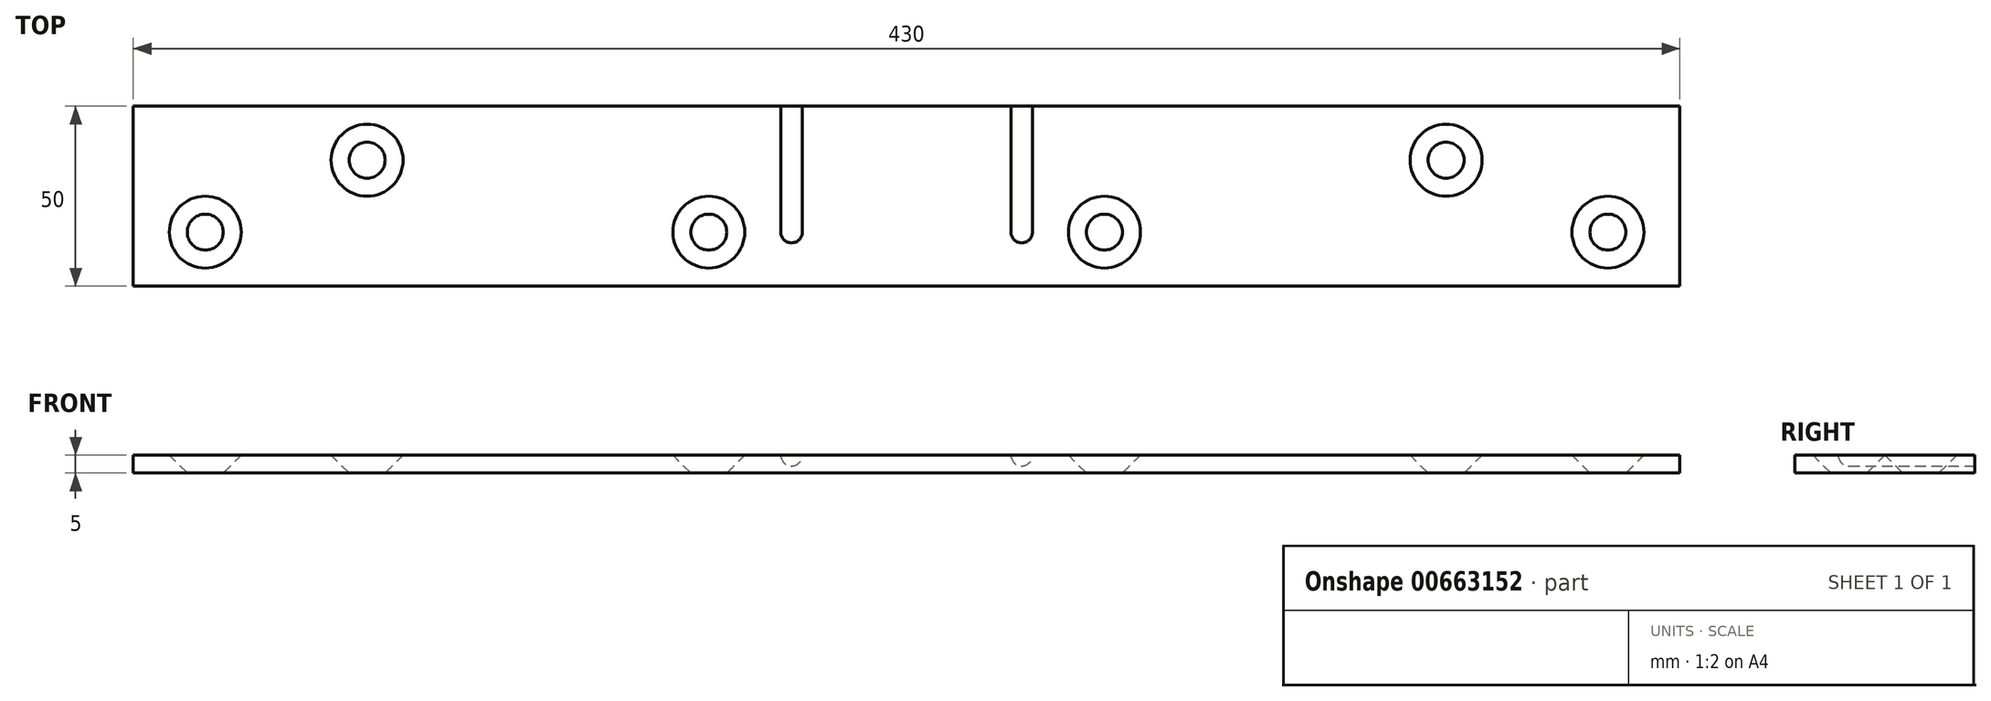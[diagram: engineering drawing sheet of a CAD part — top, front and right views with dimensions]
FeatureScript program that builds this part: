
annotation { "Feature Type Name" : "Feature", "Feature Type Description" : "" }
export const myFeature = defineFeature(function(context is Context, id is Id, definition is map)
    precondition{}
    {
        {
            var Q0;
            Q0=qCreatedBy(makeId("Top.planeOp"),FACE);
            var sketch = newSketch(context, id + "F0", { "sketchPlane" : qUnion([Q0])});
            skLineSegment(sketch, "E0.bottom", {"start": v(-215, 25) * mm, "end": v(215, 25) * mm});
            skLineSegment(sketch, "E0.top", {"start": v(-215, -25) * mm, "end": v(215, -25) * mm});
            skLineSegment(sketch, "E0.left", {"start": v(-215, 25) * mm, "end": v(-215, -25) * mm});
            skLineSegment(sketch, "E0.right", {"start": v(215, 25) * mm, "end": v(215, -25) * mm});
            skPoint(sketch, "E0.middle", {"position": v(0, 0) * mm});
            skSolve(sketch);
        }
        {
            var Q0;
            Q0=makeQuery(id+"F0.imprint","IMPRINT",FACE,{"disambiguationData":[TD([[makeQuery(id+"F0.imprint","IMPRINT",EDGE,{"derivedFrom":sQuery(id+"F0.wireOp",EDGE,"E0.bottom")}),-1.0]])]});
            extrude(context, id + "F1", {"entities" : qUnion([Q0]), "depth" : 5 * mm, "offsetDistance" : 25 * mm});
        }
        {
            var Q0;
            Q0=makeQuery(id+"F1.opExtrude","CAP_FACE",FACE,{"disambiguationData":[OSD([sQuery(id+"F0.wireOp",EDGE,"E0.bottom"),sQuery(id+"F0.wireOp",EDGE,"E0.top"),sQuery(id+"F0.wireOp",EDGE,"E0.left"),sQuery(id+"F0.wireOp",EDGE,"E0.right")])],"isStart":false});
            var sketch = newSketch(context, id + "F2", { "sketchPlane" : qUnion([Q0])});
            skCircle(sketch, "E1", {"center": v(-150, 10) * mm, "radius": 10 * mm});
            skCircle(sketch, "E2", {"center": v(-195, -10) * mm, "radius": 10 * mm});
            skCircle(sketch, "E3.1.0.0", {"center": v(-55, -10) * mm, "radius": 10 * mm});
            skLineSegment(sketch, "E3.direction1", {"start": v(-195, -10) * mm, "end": v(-55, -10) * mm, "construction": true});
            skCircle(sketch, "E4.1.0.0", {"center": v(55, -10) * mm, "radius": 10 * mm});
            skLineSegment(sketch, "E4.direction1", {"start": v(-55, -10) * mm, "end": v(55, -10) * mm, "construction": true});
            skCircle(sketch, "E5", {"center": v(195, -10) * mm, "radius": 10 * mm});
            skCircle(sketch, "E6", {"center": v(150, 10) * mm, "radius": 10 * mm});
            skSolve(sketch);
        }
        {
            var Q0;
            Q0=makeQuery(id+"F2.imprint","IMPRINT",FACE,{"disambiguationData":[TD([[makeQuery(id+"F2.imprint","IMPRINT",EDGE,{"derivedFrom":sQuery(id+"F2.wireOp",EDGE,"E1")}),1.0]])]});
            var Q1;
            Q1=makeQuery(id+"F2.imprint","IMPRINT",FACE,{"disambiguationData":[TD([[makeQuery(id+"F2.imprint","IMPRINT",EDGE,{"derivedFrom":sQuery(id+"F2.wireOp",EDGE,"E3.1.0.0")}),1.0]])]});
            var Q2;
            Q2=makeQuery(id+"F2.imprint","IMPRINT",FACE,{"disambiguationData":[TD([[makeQuery(id+"F2.imprint","IMPRINT",EDGE,{"derivedFrom":sQuery(id+"F2.wireOp",EDGE,"E2")}),1.0]])]});
            var Q3;
            Q3=makeQuery(id+"F2.imprint","IMPRINT",FACE,{"disambiguationData":[TD([[makeQuery(id+"F2.imprint","IMPRINT",EDGE,{"derivedFrom":sQuery(id+"F2.wireOp",EDGE,"E4.1.0.0")}),1.0]])]});
            var Q4;
            Q4=makeQuery(id+"F2.imprint","IMPRINT",FACE,{"disambiguationData":[TD([[makeQuery(id+"F2.imprint","IMPRINT",EDGE,{"derivedFrom":sQuery(id+"F2.wireOp",EDGE,"E5")}),1.0]])]});
            var Q5;
            Q5=makeQuery(id+"F2.imprint","IMPRINT",FACE,{"disambiguationData":[TD([[makeQuery(id+"F2.imprint","IMPRINT",EDGE,{"derivedFrom":sQuery(id+"F2.wireOp",EDGE,"E6")}),1.0]])]});
            var Q6;
            Q6=sQuery(id+"F2.wireOp",EDGE,"E1");
            extrude(context, id + "F3", {"entities" : qUnion([Q0, Q1, Q2, Q3, Q4, Q5]), "operationType" : NewBodyOperationType.REMOVE, "surfaceEntities" : qUnion([Q6]), "endBound" : BoundingType.UP_TO_NEXT, "oppositeDirection" : true, "depth" : 25 * mm, "offsetDistance" : 25 * mm, "hasDraft" : true, "draftAngle" : 45 * degree, "draftPullDirection" : true});
        }
        {
            var Q0;
            Q0=makeQuery(id+"F2.imprint","IMPRINT",FACE,{"disambiguationData":[TD([[makeQuery(id+"F2.imprint","IMPRINT",EDGE,{"derivedFrom":sQuery(id+"F2.wireOp",EDGE,"E1")}),-1.0]])]});
            var sketch = newSketch(context, id + "F4", { "sketchPlane" : qUnion([Q0])});
            skLineSegment(sketch, "E7.bottom", {"start": v(-35, 25) * mm, "end": v(-32, 25) * mm});
            skLineSegment(sketch, "E7.left", {"start": v(-35, 25) * mm, "end": v(-35, -10) * mm});
            skArc(sketch, "E8", {"start": v(-35, -10) * mm, "mid": v(-34.12, -12.12) * mm, "end": v(-32, -13) * mm});
            skLineSegment(sketch, "E9", {"start": v(-32, -13) * mm, "end": v(-32, 25) * mm});
            skSolve(sketch);
        }
        {
            var Q0;
            Q0=makeQuery(id+"F4.imprint","IMPRINT",FACE,{"disambiguationData":[TD([[makeQuery(id+"F4.imprint","IMPRINT",EDGE,{"derivedFrom":sQuery(id+"F4.wireOp",EDGE,"E7.bottom")}),-1.0]])]});
            var Q1;
            Q1=sQuery(id+"F4.wireOp",EDGE,"E9");
            revolve(context, id + "F5", {"operationType" : NewBodyOperationType.REMOVE, "entities" : qUnion([Q0]), "axis" : qUnion([Q1]), "revolveType" : RevolveType.FULL, "oppositeDirection" : true});
        }
        {
            var Q0;
            Q0=makeQuery(id+"F2.imprint","IMPRINT",FACE,{"disambiguationData":[TD([[makeQuery(id+"F2.imprint","IMPRINT",EDGE,{"derivedFrom":sQuery(id+"F2.wireOp",EDGE,"E1")}),-1.0]])]});
            var sketch = newSketch(context, id + "F6", { "sketchPlane" : qUnion([Q0])});
            skLineSegment(sketch, "E10.bottom", {"start": v(29, 25) * mm, "end": v(32, 25) * mm});
            skLineSegment(sketch, "E10.left", {"start": v(29, 25) * mm, "end": v(29, -10) * mm});
            skArc(sketch, "E11", {"start": v(29, -10) * mm, "mid": v(29.88, -12.12) * mm, "end": v(32, -13) * mm});
            skLineSegment(sketch, "E12", {"start": v(32, -13) * mm, "end": v(32, 25) * mm});
            skSolve(sketch);
        }
        {
            var Q0;
            Q0=makeQuery(id+"F6.imprint","IMPRINT",FACE,{"disambiguationData":[TD([[makeQuery(id+"F6.imprint","IMPRINT",EDGE,{"derivedFrom":sQuery(id+"F6.wireOp",EDGE,"E10.bottom")}),-1.0]])]});
            var Q1;
            Q1=sQuery(id+"F6.wireOp",EDGE,"E10.bottom");
            var Q2;
            Q2=sQuery(id+"F6.wireOp",EDGE,"E11");
            var Q3;
            Q3=sQuery(id+"F6.wireOp",EDGE,"E10.left");
            var Q4;
            Q4=sQuery(id+"F6.wireOp",EDGE,"E12");
            var Q5;
            Q5=sQuery(id+"F6.wireOp",EDGE,"E12");
            revolve(context, id + "F7", {"operationType" : NewBodyOperationType.REMOVE, "entities" : qUnion([Q0]), "surfaceEntities" : qUnion([Q1, Q2, Q3, Q4]), "axis" : qUnion([Q5]), "revolveType" : RevolveType.FULL, "oppositeDirection" : true});
        }
    });
